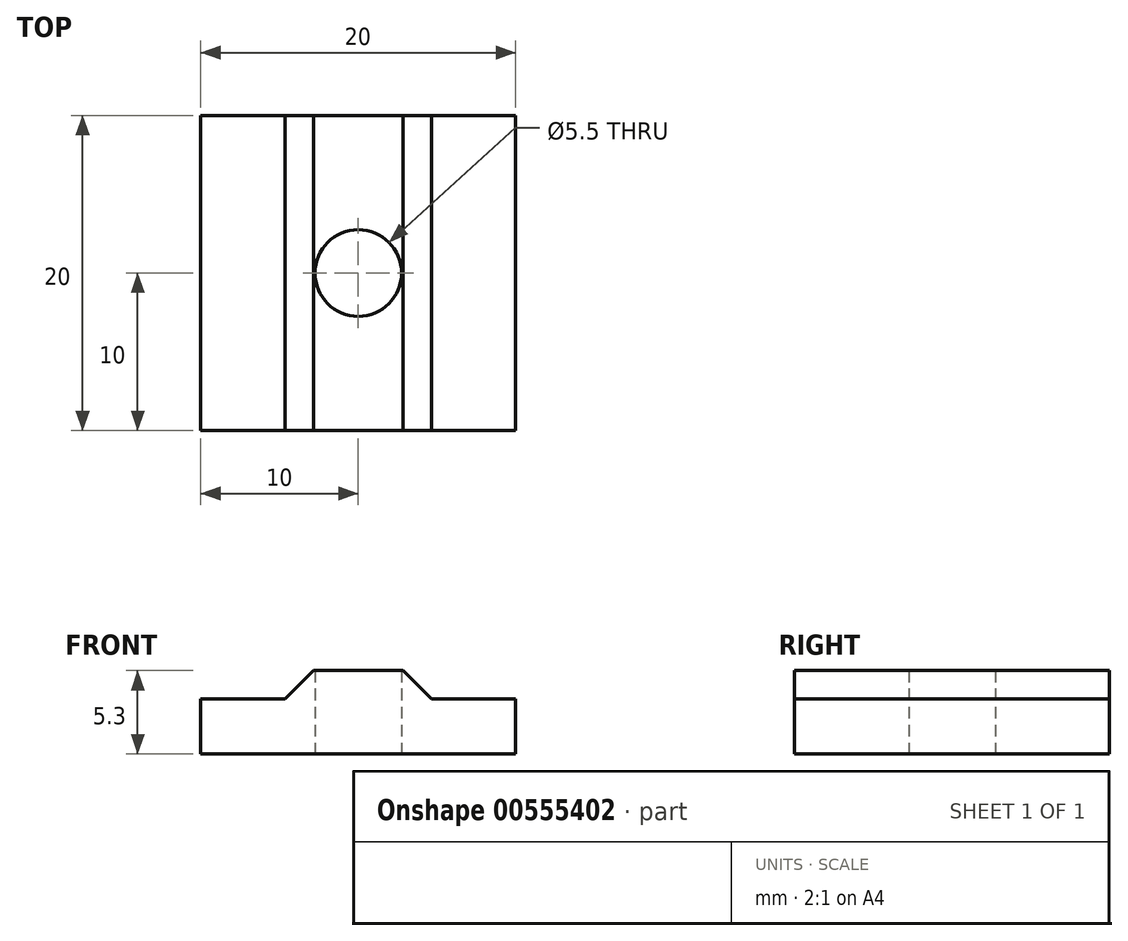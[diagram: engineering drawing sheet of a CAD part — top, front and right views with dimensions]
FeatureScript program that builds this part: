
annotation { "Feature Type Name" : "Feature", "Feature Type Description" : "" }
export const myFeature = defineFeature(function(context is Context, id is Id, definition is map)
    precondition{}
    {
        {
            var Q0;
            Q0=qCreatedBy(makeId("Front.planeOp"),FACE);
            var sketch = newSketch(context, id + "F0", { "sketchPlane" : qUnion([Q0])});
            skLineSegment(sketch, "E0", {"start": v(-10, 0) * mm, "end": v(10, 0) * mm});
            skLineSegment(sketch, "E1", {"start": v(10, 0) * mm, "end": v(10, 3.5) * mm});
            skLineSegment(sketch, "E2", {"start": v(10, 3.5) * mm, "end": v(4.64, 3.5) * mm});
            skLineSegment(sketch, "E3", {"start": v(4.64, 3.5) * mm, "end": v(2.84, 5.3) * mm});
            skLineSegment(sketch, "E4", {"start": v(2.84, 5.3) * mm, "end": v(-2.84, 5.3) * mm});
            skLineSegment(sketch, "E5", {"start": v(0, 0) * mm, "end": v(0, 5.3) * mm, "construction": true});
            skLineSegment(sketch, "E6.MirrorCS", {"start": v(-4.64, 3.5) * mm, "end": v(-2.84, 5.3) * mm});
            skLineSegment(sketch, "E7.MirrorCS", {"start": v(-10, 3.5) * mm, "end": v(-4.64, 3.5) * mm});
            skLineSegment(sketch, "E8.MirrorCS", {"start": v(-10, 0) * mm, "end": v(-10, 3.5) * mm});
            skSolve(sketch);
        }
        {
            var Q0;
            Q0 = qSketchRegion(id + "F0", true);
            extrude(context, id + "F1", {"entities" : qUnion([Q0]), "depth" : 20 * mm, "offsetDistance" : 25 * mm, "symmetric" : true});
        }
        {
            var Q0;
            Q0=makeQuery(id+"F1.opExtrude","SWEPT_FACE",FACE,{"disambiguationData":[OSD([sQuery(id+"F0.wireOp",EDGE,"E0")])]});
            var sketch = newSketch(context, id + "F2", { "sketchPlane" : qUnion([Q0])});
            skCircle(sketch, "E9", {"center": v(0, 0) * mm, "radius": 2.75 * mm});
            skSolve(sketch);
        }
        {
            var Q0;
            Q0 = qSketchRegion(id + "F2", true);
            extrude(context, id + "F3", {"entities" : qUnion([Q0]), "operationType" : NewBodyOperationType.REMOVE, "endBound" : BoundingType.THROUGH_ALL, "oppositeDirection" : true, "depth" : 25 * mm, "offsetDistance" : 25 * mm});
        }
    });
